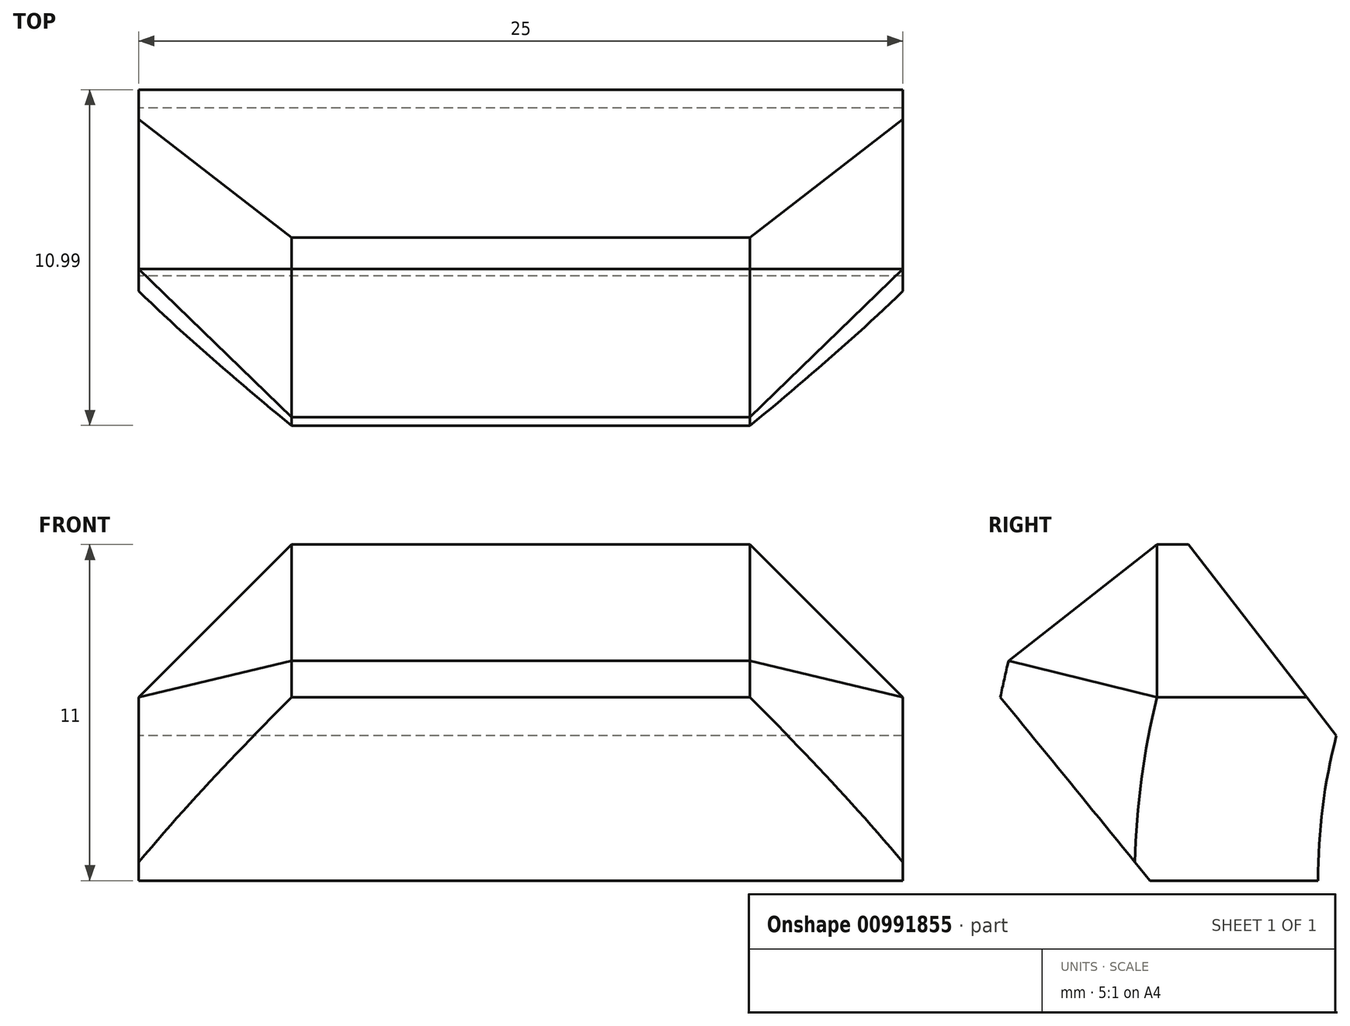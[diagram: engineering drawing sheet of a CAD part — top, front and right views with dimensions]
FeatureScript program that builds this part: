
annotation { "Feature Type Name" : "Feature", "Feature Type Description" : "" }
export const myFeature = defineFeature(function(context is Context, id is Id, definition is map)
    precondition{}
    {
        {
            var Q0;
            Q0=qCreatedBy(makeId("Right.planeOp"),FACE);
            var sketch = newSketch(context, id + "F0", { "sketchPlane" : qUnion([Q0])});
            skCircle(sketch, "E0", {"center": v(0, 0) * mm, "radius": 19 * mm});
            skCircle(sketch, "E1", {"center": v(0, 0) * mm, "radius": 30 * mm});
            skLineSegment(sketch, "E2.bottom", {"start": v(-56, 0) * mm, "end": v(51, 0) * mm});
            skLineSegment(sketch, "E2.top", {"start": v(-56, 11) * mm, "end": v(51, 11) * mm});
            skLineSegment(sketch, "E2.left", {"start": v(-56, 0) * mm, "end": v(-56, 11) * mm});
            skLineSegment(sketch, "E2.right", {"start": v(51, 0) * mm, "end": v(51, 11) * mm});
            skLineSegment(sketch, "E3.bottom", {"start": v(51, 11) * mm, "end": v(40, 11) * mm});
            skLineSegment(sketch, "E3.top", {"start": v(51, 41) * mm, "end": v(40, 41) * mm});
            skLineSegment(sketch, "E3.left", {"start": v(51, 11) * mm, "end": v(51, 41) * mm});
            skLineSegment(sketch, "E3.right", {"start": v(40, 11) * mm, "end": v(40, 41) * mm});
            skSolve(sketch);
        }
        {
            var Q0;
            {var subQ0=sQuery(id+"F0.wireOp",EDGE,"E2.top");var subQ1=sQuery(id+"F0.wireOp",EDGE,"E0");var subQ2=makeQuery(id+"F0.imprint","INTERSECT",VERTEX,{"disambiguationData":[OD(0.0)],"derivedFrom":[subQ1,subQ0]});Q0=makeQuery(id+"F0.imprint","IMPRINT",FACE,{"disambiguationData":[TD([[makeQuery(id+"F0.imprint","IMPRINT",EDGE,{"disambiguationData":[TD([[subQ2,-1.0]])],"derivedFrom":subQ1}),-1.0]])]});}
            extrude(context, id + "F1", {"entities" : qUnion([Q0]), "depth" : 25 * mm, "offsetDistance" : 25 * mm});
        }
        {
            var Q0;
            {var subQ0=sQuery(id+"F0.wireOp",EDGE,"E2.top");Q0=makeQuery(id+"F1.opExtrude","SWEPT_FACE",FACE,{"disambiguationData":[OSD([subQ0]),TDD([makeQuery(id+"F0.imprint","IMPRINT",EDGE,{"disambiguationData":[TD([[makeQuery(id+"F0.imprint","INTERSECT",VERTEX,{"disambiguationData":[OD(0.0)],"derivedFrom":[sQuery(id+"F0.wireOp",EDGE,"E1"),subQ0]}),1.0]])],"derivedFrom":subQ0})])]});}
            var Q1;
            {var subQ0=sQuery(id+"F0.wireOp",EDGE,"E2.top");Q1=makeQuery(id+"F1.opExtrude","SWEPT_FACE",FACE,{"disambiguationData":[OSD([subQ0]),TDD([makeQuery(id+"F0.imprint","IMPRINT",EDGE,{"disambiguationData":[TD([[makeQuery(id+"F0.imprint","INTERSECT",VERTEX,{"disambiguationData":[OD(1.0)],"derivedFrom":[sQuery(id+"F0.wireOp",EDGE,"E1"),subQ0]}),-1.0]])],"derivedFrom":subQ0})])]});}
            var Q2;
            Q2=makeQuery(id+"F1.opExtrude","SWEPT_FACE",FACE,{"disambiguationData":[OSD([sQuery(id+"F0.wireOp",EDGE,"E1")])]});
            chamfer(context, id + "F2", {"entities" : qUnion([Q0, Q1, Q2]), "width" : 5 * mm, "tangentPropagation" : true});
        }
    });
